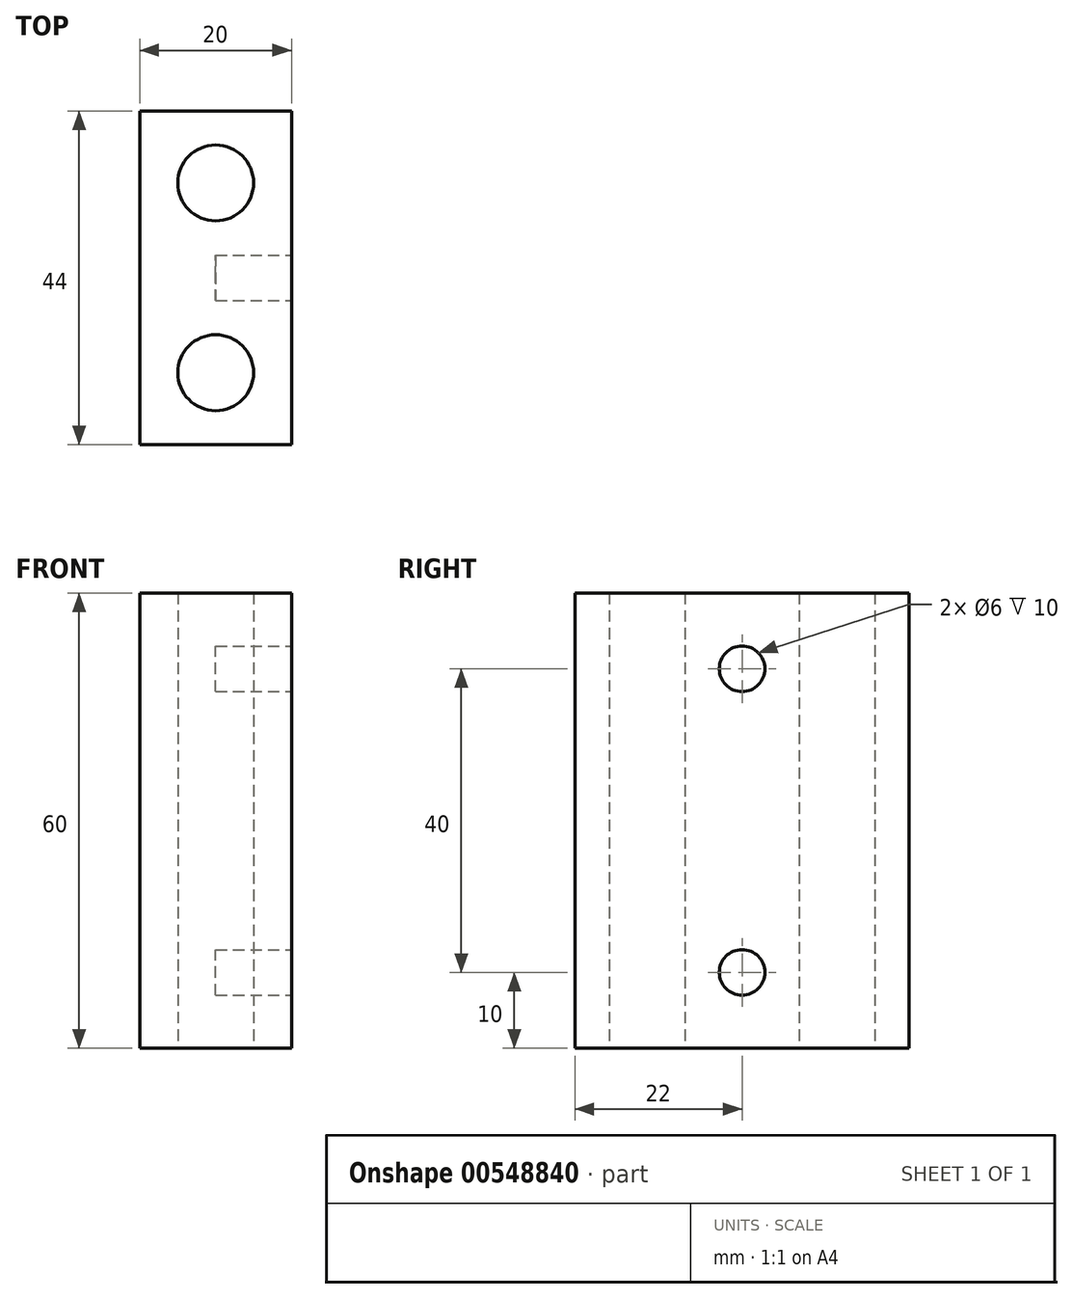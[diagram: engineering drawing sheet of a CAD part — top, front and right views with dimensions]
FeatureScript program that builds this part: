
annotation { "Feature Type Name" : "Feature", "Feature Type Description" : "" }
export const myFeature = defineFeature(function(context is Context, id is Id, definition is map)
    precondition{}
    {
        {
            var Q0;
            Q0=qCreatedBy(makeId("Top.planeOp"),FACE);
            var sketch = newSketch(context, id + "F0", { "sketchPlane" : qUnion([Q0])});
            skCircle(sketch, "E0", {"center": v(0, 12.5) * mm, "radius": 5 * mm});
            skCircle(sketch, "E1", {"center": v(0, -12.5) * mm, "radius": 5 * mm});
            skLineSegment(sketch, "E2.bottom", {"start": v(-10, 22) * mm, "end": v(10, 22) * mm});
            skLineSegment(sketch, "E2.top", {"start": v(-10, -22) * mm, "end": v(10, -22) * mm});
            skLineSegment(sketch, "E2.left", {"start": v(-10, 22) * mm, "end": v(-10, -22) * mm});
            skLineSegment(sketch, "E2.right", {"start": v(10, 22) * mm, "end": v(10, -22) * mm});
            skSolve(sketch);
        }
        {
            var Q0;
            Q0=qSketchRegion(id+"F0",true);
            extrude(context, id + "F1", {"entities" : qUnion([Q0]), "depth" : 60 * mm, "offsetDistance" : 25 * mm});
        }
        {
            var Q0;
            Q0=makeQuery(id+"F1.opExtrude","SWEPT_FACE",FACE,{"disambiguationData":[OSD([sQuery(id+"F0.wireOp",EDGE,"E2.right")])]});
            var sketch = newSketch(context, id + "F2", { "sketchPlane" : qUnion([Q0])});
            skLineSegment(sketch, "E3", {"start": v(22, 30) * mm, "end": v(-22, 30) * mm, "construction": true});
            skLineSegment(sketch, "E4", {"start": v(0, 60) * mm, "end": v(0, 0) * mm, "construction": true});
            skCircle(sketch, "E5", {"center": v(0, 50) * mm, "radius": 3 * mm});
            skCircle(sketch, "E6", {"center": v(0, 10) * mm, "radius": 3 * mm});
            skSolve(sketch);
        }
        {
            var Q0;
            Q0=qSketchRegion(id+"F2",true);
            extrude(context, id + "F3", {"entities" : qUnion([Q0]), "operationType" : NewBodyOperationType.REMOVE, "oppositeDirection" : true, "depth" : 10 * mm, "offsetDistance" : 25 * mm});
        }
    });
